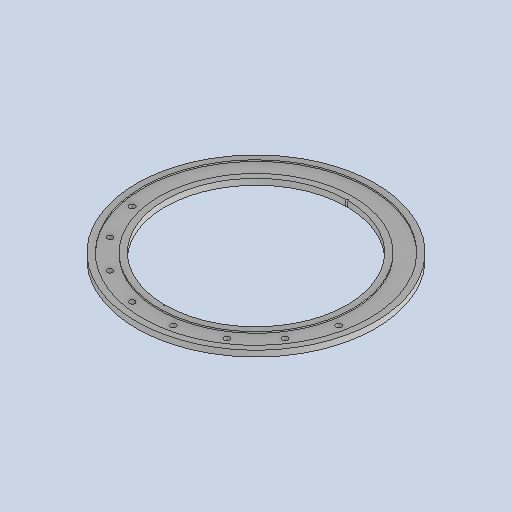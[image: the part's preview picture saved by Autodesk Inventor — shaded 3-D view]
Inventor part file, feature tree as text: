
AUTODESK INVENTOR PART (.ipt)
format: ipt  version: 2025 (Build 290162010, 162A)  size: 220,160 bytes
history: native  units: mm
features: extrude x4, sketch x4, pattern_circular x1, mirror x1, projected_geometry x1, other x1
ambient origin geometry x8: Origin, YZ Plane, XZ Plane, XY Plane, X Axis, Y Axis, Z Axis, Center Point
bodies: Solid1 (feature_tree)
feature tree (12):
  extrude  "Extrusion1"  Depth=15.0mm
  extrude  "Extrusion2"  TaperAngle=0.0deg  [1 undecoded]
  extrude  "Extrusion3"  Depth=72.0mm
  pattern_circular  "Circular Pattern2"  Count=53  [1 undecoded]
  extrude  "Extrusion4"  Depth=14.0mm
  mirror  "Mirror1"
  sketch  "Sketch1"  dims[d2=15.0mm d3=0.0mm d4=42.0mm]
  sketch  "Sketch2"  dims[d6=3.5mm d7=0.0mm d10=0.0mm d11=0.0mm]
  projected_geometry  "Projected Loop1"
  sketch  "Sketch3"  dims[d17=530.0mm d18=72.0mm d19=530.0mm]
  sketch  "Sketch5"  dims[d20=1.963495mm d21=14.0mm d22=80.0mm d23=157.5deg d34=0.0mm d35=0.0mm d40=5.0mm]
  other  "Definition1"
note: 2 required parameter values undecoded (feature->parameter linkage not recoverable at this tier; creation-order binding heuristic only, values carry confidence <= 0.55)
